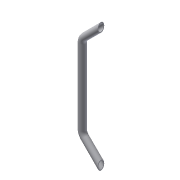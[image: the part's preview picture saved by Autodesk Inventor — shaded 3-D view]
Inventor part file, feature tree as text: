
AUTODESK INVENTOR PART (.ipt)
format: ipt  version: 2015 (Build 190159000, 159)  size: 141,312 bytes
history: native  units: mm
features: sketch x4, other x3, extrude x2, shell x1
ambient origin geometry x8: Origin, YZ Plane, XZ Plane, XY Plane, X Axis, Y Axis, Z Axis, Center Point
bodies: Body1 (feature_tree)
feature tree (10):
  other  "Bryła1"
  extrude  "Wyciągnięcie proste1"  Depth=20.0mm
  shell  "Skorupa1"  Thickness=430.0mm
  other  "Gięcie części1"
  other  "Gięcie części2"
  extrude  "Wyciągnięcie proste3"  Depth=2.0mm
  sketch  "Szkic1"
  sketch  "Szkic2"
  sketch  "Szkic3"
  sketch  "Szkic4"
